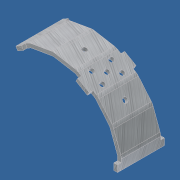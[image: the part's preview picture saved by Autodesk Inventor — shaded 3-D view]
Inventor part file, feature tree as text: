
AUTODESK INVENTOR PART (.ipt)
format: ipt  version: 2011 (Build 150239000, 239)  size: 209,920 bytes
history: native  units: in
note: dims shown in document units (in); Inventor stores cm internally (conversion verified against a paired STEP export)
features: extrude x4, sketch x3, mirror x2, fillet x1
ambient origin geometry x8: Origin, YZ Plane, XZ Plane, XY Plane, X Axis, Y Axis, Z Axis, Center Point
bodies: Solid1 (feature_tree)
feature tree (10):
  sketch  "Sketch1"  dims[d2=0.095in d8=0.095in]
  extrude  "Extrusion1"  Depth=0.095in
  extrude  "Extrusion2"  Depth=0.095in
  extrude  "Extrusion3"  Depth=0.1675in
  extrude  "Extrusion4"  Depth=0.1675in
  fillet  "Fillet1"  Radius=0.095in
  mirror  "Mirror5"
  mirror  "Mirror6"
  sketch  "Sketch2"  dims[d9=0.095in d10=0.095in]
  sketch  "Sketch3"  dims[d21=0.5in d22=0.0in d23=0.1675in d24=0.1675in d25=0.095in d26=0.0in d27=0.125in d28=0.095in d29=0.0in d30=0.125in d31=0.0in d32=0.125in d33=0.25in d34=0.1562in d35=0.095in d36=0.0in d37=0.25in d38=0.125in d41=3.25in d44=60.0deg]
